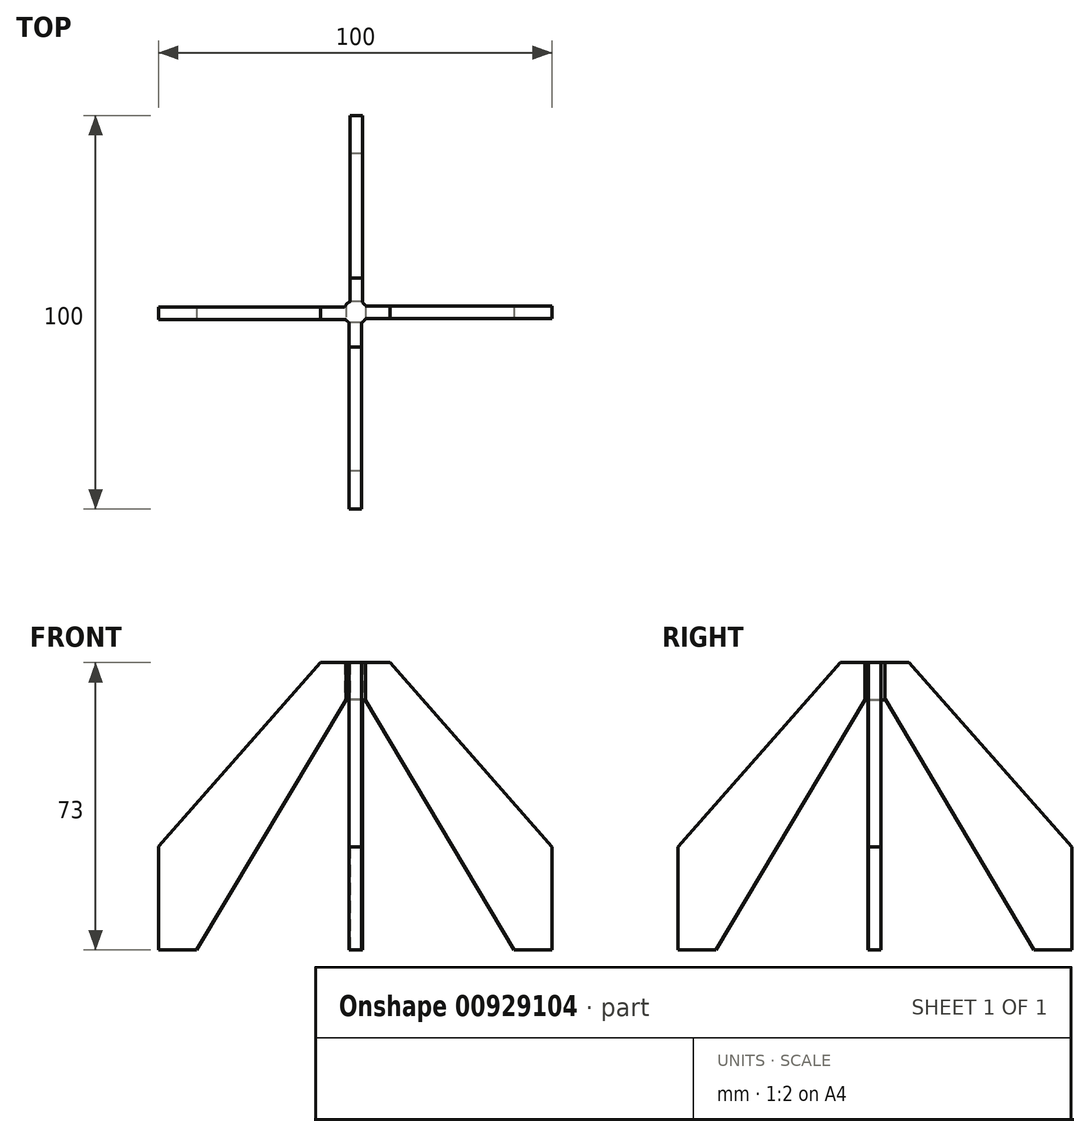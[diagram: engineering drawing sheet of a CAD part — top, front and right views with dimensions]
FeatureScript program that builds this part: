
annotation { "Feature Type Name" : "Feature", "Feature Type Description" : "" }
export const myFeature = defineFeature(function(context is Context, id is Id, definition is map)
    precondition{}
    {
        {
            var Q0;
            Q0=qCreatedBy(makeId("Top.planeOp"),FACE);
            var sketch = newSketch(context, id + "F0", { "sketchPlane" : qUnion([Q0])});
            skCircle(sketch, "E0", {"center": v(0, 0) * mm, "radius": 3.05 * mm});
            skSolve(sketch);
        }
        {
            var Q0;
            Q0=makeQuery(id+"F0.imprint","IMPRINT",FACE,{"disambiguationData":[TD([[makeQuery(id+"F0.imprint","IMPRINT",EDGE,{"derivedFrom":sQuery(id+"F0.wireOp",EDGE,"E0")}),1.0]])]});
            extrude(context, id + "F1", {"entities" : qUnion([Q0]), "depth" : 110 * mm, "offsetDistance" : 25.4 * mm});
        }
        {
            var Q0;
            Q0=qCreatedBy(makeId("Top.planeOp"),FACE);
            var sketch = newSketch(context, id + "F2", { "sketchPlane" : qUnion([Q0])});
            skLineSegment(sketch, "E1.bottom", {"start": v(1.6, 0) * mm, "end": v(-1.58, 0) * mm});
            skLineSegment(sketch, "E1.top", {"start": v(1.6, -50) * mm, "end": v(-1.58, -50) * mm});
            skLineSegment(sketch, "E1.left", {"start": v(1.6, 0) * mm, "end": v(1.6, -50) * mm});
            skLineSegment(sketch, "E1.right", {"start": v(-1.58, 0) * mm, "end": v(-1.58, -50) * mm});
            skSolve(sketch);
        }
        {
            var Q0;
            Q0=makeQuery(id+"F2.imprint","IMPRINT",FACE,{"disambiguationData":[TD([[makeQuery(id+"F2.imprint","IMPRINT",EDGE,{"derivedFrom":sQuery(id+"F2.wireOp",EDGE,"E1.bottom")}),1.0]])]});
            extrude(context, id + "F3", {"entities" : qUnion([Q0]), "operationType" : NewBodyOperationType.ADD, "depth" : 80 * mm, "offsetDistance" : 25.4 * mm});
        }
        {
            var Q0;
            Q0=makeQuery(id+"F3.opExtrude","SWEPT_FACE",FACE,{"disambiguationData":[OSD([sQuery(id+"F2.wireOp",EDGE,"E1.right")])]});
            var sketch = newSketch(context, id + "F4", { "sketchPlane" : qUnion([Q0])});
            skLineSegment(sketch, "E2", {"start": v(2.6, 80) * mm, "end": v(50, 26.2) * mm});
            skSolve(sketch);
        }
        {
            var Q0;
            {var subQ0=sQuery(id+"F4.wireOp",EDGE,"E2");Q0=makeQuery(id+"F4.imprint","IMPRINT",FACE,{"disambiguationData":[TD([[makeQuery(id+"F4.imprint","IMPRINT",EDGE,{"derivedFrom":subQ0}),1.0]])]});}
            extrude(context, id + "F5", {"entities" : qUnion([Q0]), "operationType" : NewBodyOperationType.REMOVE, "endBound" : BoundingType.UP_TO_NEXT, "oppositeDirection" : true, "depth" : 25.4 * mm, "offsetDistance" : 25.4 * mm});
        }
        {
            var Q0;
            Q0=qCreatedBy(makeId("Top.planeOp"),FACE);
            var sketch = newSketch(context, id + "F6", { "sketchPlane" : qUnion([Q0])});
            skLineSegment(sketch, "E3.bottom", {"start": v(0, 1.57) * mm, "end": v(50, 1.57) * mm});
            skLineSegment(sketch, "E3.top", {"start": v(0, -1.6) * mm, "end": v(50, -1.6) * mm});
            skLineSegment(sketch, "E3.left", {"start": v(0, 1.57) * mm, "end": v(0, -1.6) * mm});
            skLineSegment(sketch, "E3.right", {"start": v(50, 1.57) * mm, "end": v(50, -1.6) * mm});
            skSolve(sketch);
        }
        {
            var Q0;
            Q0=makeQuery(id+"F6.imprint","IMPRINT",FACE,{"disambiguationData":[TD([[makeQuery(id+"F6.imprint","IMPRINT",EDGE,{"derivedFrom":sQuery(id+"F6.wireOp",EDGE,"E3.bottom")}),-1.0]])]});
            extrude(context, id + "F7", {"entities" : qUnion([Q0]), "operationType" : NewBodyOperationType.ADD, "depth" : 80 * mm, "offsetDistance" : 25.4 * mm});
        }
        {
            var Q0;
            Q0=makeQuery(id+"F7.opExtrude","SWEPT_FACE",FACE,{"disambiguationData":[OSD([sQuery(id+"F6.wireOp",EDGE,"E3.top")])]});
            var sketch = newSketch(context, id + "F8", { "sketchPlane" : qUnion([Q0])});
            skLineSegment(sketch, "E4", {"start": v(2.59, 80) * mm, "end": v(2.59, 26.17) * mm});
            skLineSegment(sketch, "E5", {"start": v(2.59, 26.17) * mm, "end": v(50, 26.17) * mm});
            skLineSegment(sketch, "E6", {"start": v(50, 26.17) * mm, "end": v(2.59, 80) * mm});
            skSolve(sketch);
        }
        {
            var Q0;
            {var subQ0=sQuery(id+"F8.wireOp",EDGE,"E6");Q0=makeQuery(id+"F8.imprint","IMPRINT",FACE,{"disambiguationData":[TD([[makeQuery(id+"F8.imprint","IMPRINT",EDGE,{"derivedFrom":subQ0}),-1.0]])]});}
            extrude(context, id + "F9", {"entities" : qUnion([Q0]), "operationType" : NewBodyOperationType.REMOVE, "endBound" : BoundingType.UP_TO_NEXT, "oppositeDirection" : true, "depth" : 25.4 * mm, "offsetDistance" : 25.4 * mm});
        }
        {
            var Q0;
            Q0=qCreatedBy(makeId("Top.planeOp"),FACE);
            var sketch = newSketch(context, id + "F10", { "sketchPlane" : qUnion([Q0])});
            skLineSegment(sketch, "E7.bottom", {"start": v(1.78, 0) * mm, "end": v(-1.4, 0) * mm});
            skLineSegment(sketch, "E7.top", {"start": v(1.78, 50) * mm, "end": v(-1.4, 50) * mm});
            skLineSegment(sketch, "E7.left", {"start": v(1.78, 0) * mm, "end": v(1.78, 50) * mm});
            skLineSegment(sketch, "E7.right", {"start": v(-1.4, 0) * mm, "end": v(-1.4, 50) * mm});
            skSolve(sketch);
        }
        {
            var Q0;
            Q0=makeQuery(id+"F10.imprint","IMPRINT",FACE,{"disambiguationData":[TD([[makeQuery(id+"F10.imprint","IMPRINT",EDGE,{"derivedFrom":sQuery(id+"F10.wireOp",EDGE,"E7.bottom")}),-1.0]])]});
            extrude(context, id + "F11", {"entities" : qUnion([Q0]), "operationType" : NewBodyOperationType.ADD, "depth" : 80 * mm, "offsetDistance" : 25.4 * mm});
        }
        {
            var Q0;
            Q0=makeQuery(id+"F11.opExtrude","SWEPT_FACE",FACE,{"disambiguationData":[OSD([sQuery(id+"F10.wireOp",EDGE,"E7.left")])]});
            var sketch = newSketch(context, id + "F12", { "sketchPlane" : qUnion([Q0])});
            skLineSegment(sketch, "E8", {"start": v(2.48, 80) * mm, "end": v(2.48, 26.2) * mm});
            skLineSegment(sketch, "E9", {"start": v(2.48, 26.2) * mm, "end": v(50, 26.2) * mm});
            skLineSegment(sketch, "E10", {"start": v(50, 26.2) * mm, "end": v(2.48, 80) * mm});
            skSolve(sketch);
        }
        {
            var Q0;
            {var subQ0=sQuery(id+"F12.wireOp",EDGE,"E10");Q0=makeQuery(id+"F12.imprint","IMPRINT",FACE,{"disambiguationData":[TD([[makeQuery(id+"F12.imprint","IMPRINT",EDGE,{"derivedFrom":subQ0}),-1.0]])]});}
            extrude(context, id + "F13", {"entities" : qUnion([Q0]), "operationType" : NewBodyOperationType.REMOVE, "endBound" : BoundingType.UP_TO_NEXT, "oppositeDirection" : true, "depth" : 25.4 * mm, "offsetDistance" : 25.4 * mm});
        }
        {
            var Q0;
            Q0=qCreatedBy(makeId("Top.planeOp"),FACE);
            var sketch = newSketch(context, id + "F14", { "sketchPlane" : qUnion([Q0])});
            skLineSegment(sketch, "E11.bottom", {"start": v(0, -1.84) * mm, "end": v(-50, -1.84) * mm});
            skLineSegment(sketch, "E11.top", {"start": v(0, 1.34) * mm, "end": v(-50, 1.34) * mm});
            skLineSegment(sketch, "E11.left", {"start": v(0, -1.84) * mm, "end": v(0, 1.34) * mm});
            skLineSegment(sketch, "E11.right", {"start": v(-50, -1.84) * mm, "end": v(-50, 1.34) * mm});
            skSolve(sketch);
        }
        {
            var Q0;
            Q0=makeQuery(id+"F14.imprint","IMPRINT",FACE,{"disambiguationData":[TD([[makeQuery(id+"F14.imprint","IMPRINT",EDGE,{"derivedFrom":sQuery(id+"F14.wireOp",EDGE,"E11.bottom")}),-1.0]])]});
            extrude(context, id + "F15", {"entities" : qUnion([Q0]), "operationType" : NewBodyOperationType.ADD, "depth" : 80 * mm, "offsetDistance" : 25.4 * mm});
        }
        {
            var Q0;
            Q0=makeQuery(id+"F15.opExtrude","SWEPT_FACE",FACE,{"disambiguationData":[OSD([sQuery(id+"F14.wireOp",EDGE,"E11.top")])]});
            var sketch = newSketch(context, id + "F16", { "sketchPlane" : qUnion([Q0])});
            skLineSegment(sketch, "E12", {"start": v(2.74, 80) * mm, "end": v(2.74, 26.27) * mm});
            skLineSegment(sketch, "E13", {"start": v(2.74, 26.27) * mm, "end": v(50, 26.27) * mm});
            skLineSegment(sketch, "E14", {"start": v(50, 26.27) * mm, "end": v(2.74, 80) * mm});
            skSolve(sketch);
        }
        {
            var Q0;
            {var subQ0=sQuery(id+"F16.wireOp",EDGE,"E14");Q0=makeQuery(id+"F16.imprint","IMPRINT",FACE,{"disambiguationData":[TD([[makeQuery(id+"F16.imprint","IMPRINT",EDGE,{"derivedFrom":subQ0}),-1.0]])]});}
            extrude(context, id + "F17", {"entities" : qUnion([Q0]), "operationType" : NewBodyOperationType.REMOVE, "endBound" : BoundingType.UP_TO_NEXT, "oppositeDirection" : true, "depth" : 25.4 * mm, "offsetDistance" : 25.4 * mm});
        }
        {
            var Q0;
            Q0=makeQuery(id+"F1.opExtrude","CAP_FACE",FACE,{"disambiguationData":[OSD([sQuery(id+"F0.wireOp",EDGE,"E0")])],"isStart":false});
            var sketch = newSketch(context, id + "F18", { "sketchPlane" : qUnion([Q0])});
            skCircle(sketch, "E15", {"center": v(0, 0) * mm, "radius": 5.3 * mm});
            skSolve(sketch);
        }
        {
            var Q0;
            Q0=qSketchRegion(id+"F18",true);
            extrude(context, id + "F19", {"entities" : qUnion([Q0]), "operationType" : NewBodyOperationType.ADD, "depth" : 5 * mm, "offsetDistance" : 25.4 * mm});
        }
        {
            var Q0;
            Q0=makeQuery(id+"F19.opExtrude","CAP_FACE",FACE,{"disambiguationData":[OSD([sQuery(id+"F18.wireOp",EDGE,"E15")])],"isStart":false});
            var sketch = newSketch(context, id + "F20", { "sketchPlane" : qUnion([Q0])});
            skSolve(sketch);
        }
        {
            var Q0;
            Q0=makeQuery(id+"F19.opExtrude","CAP_EDGE",EDGE,{"disambiguationData":[OSD([sQuery(id+"F18.wireOp",EDGE,"E15")])],"isStart":true});
            fillet(context, id + "F21", {"entities" : qUnion([Q0]), "radius" : 5.08 * mm, "tangentPropagation" : true, "allowEdgeOverflow" : false});
        }
        {
            var Q0;
            Q0=makeQuery(id+"F20.imprint","IMPRINT",FACE,{"disambiguationData":[TD([[makeQuery(id+"F20.imprint","IMPRINT",EDGE,{"derivedFrom":makeQuery(id+"F19.opExtrude","CAP_EDGE",EDGE,{"disambiguationData":[OSD([sQuery(id+"F18.wireOp",EDGE,"E15")])],"isStart":false})}),1.0]])]});
            var sketch = newSketch(context, id + "F22", { "sketchPlane" : qUnion([Q0])});
            skCircle(sketch, "E16", {"center": v(0, 0) * mm, "radius": 9.43 * mm});
            skSolve(sketch);
        }
        {
            var Q0;
            Q0=makeQuery(id+"F22.imprint","IMPRINT",FACE,{"disambiguationData":[TD([[makeQuery(id+"F22.imprint","IMPRINT",EDGE,{"derivedFrom":sQuery(id+"F22.wireOp",EDGE,"E16")}),1.0]])]});
            var Q1;
            Q1=makeQuery(id+"F20.imprint","IMPRINT",FACE,{"disambiguationData":[TD([[makeQuery(id+"F20.imprint","IMPRINT",EDGE,{"derivedFrom":makeQuery(id+"F19.opExtrude","CAP_EDGE",EDGE,{"disambiguationData":[OSD([sQuery(id+"F18.wireOp",EDGE,"E15")])],"isStart":false})}),1.0]])]});
            extrude(context, id + "F23", {"entities" : qUnion([Q0, Q1]), "operationType" : NewBodyOperationType.REMOVE, "oppositeDirection" : true, "depth" : 42 * mm, "offsetDistance" : 25.4 * mm});
        }
        {
            var Q0;
            Q0=makeQuery(id+"F7.opExtrude","SWEPT_FACE",FACE,{"disambiguationData":[OSD([sQuery(id+"F6.wireOp",EDGE,"E3.top")])]});
            var sketch = newSketch(context, id + "F24", { "sketchPlane" : qUnion([Q0])});
            skLineSegment(sketch, "E17", {"start": v(2.59, 0) * mm, "end": v(2.59, 51.3) * mm});
            skLineSegment(sketch, "E18", {"start": v(2.59, 63.43) * mm, "end": v(40.35, 0) * mm});
            skLineSegment(sketch, "E19", {"start": v(50, 0) * mm, "end": v(40.35, 0) * mm, "construction": true});
            skSolve(sketch);
        }
        {
            var Q0;
            {var subQ0=sQuery(id+"F24.wireOp",EDGE,"E17");Q0=makeQuery(id+"F24.imprint","IMPRINT",FACE,{"disambiguationData":[TD([[makeQuery(id+"F24.imprint","IMPRINT",EDGE,{"derivedFrom":subQ0}),1.0]])]});}
            extrude(context, id + "F25", {"entities" : qUnion([Q0]), "operationType" : NewBodyOperationType.REMOVE, "endBound" : BoundingType.UP_TO_NEXT, "oppositeDirection" : true, "depth" : 25.4 * mm, "offsetDistance" : 25.4 * mm});
        }
        {
            var Q0;
            Q0=makeQuery(id+"F15.opExtrude","SWEPT_FACE",FACE,{"disambiguationData":[OSD([sQuery(id+"F14.wireOp",EDGE,"E11.bottom")])]});
            var sketch = newSketch(context, id + "F26", { "sketchPlane" : qUnion([Q0])});
            skLineSegment(sketch, "E20", {"start": v(-50, 13.13) * mm, "end": v(-40.34, 13.13) * mm, "construction": true});
            skLineSegment(sketch, "E21", {"start": v(-40.34, 0) * mm, "end": v(-2.43, 63.57) * mm});
            skSolve(sketch);
        }
        {
            var Q0;
            {var subQ0=sQuery(id+"F26.wireOp",EDGE,"E21");Q0=makeQuery(id+"F26.imprint","IMPRINT",FACE,{"disambiguationData":[TD([[makeQuery(id+"F26.imprint","IMPRINT",EDGE,{"derivedFrom":subQ0}),-1.0]])]});}
            extrude(context, id + "F27", {"entities" : qUnion([Q0]), "operationType" : NewBodyOperationType.REMOVE, "endBound" : BoundingType.UP_TO_NEXT, "oppositeDirection" : true, "depth" : 25.4 * mm, "offsetDistance" : 25.4 * mm});
        }
        {
            var Q0;
            Q0=makeQuery(id+"F3.opExtrude","SWEPT_FACE",FACE,{"disambiguationData":[OSD([sQuery(id+"F2.wireOp",EDGE,"E1.right")])]});
            var sketch = newSketch(context, id + "F28", { "sketchPlane" : qUnion([Q0])});
            skLineSegment(sketch, "E22", {"start": v(50, 9.83) * mm, "end": v(40.35, 9.83) * mm, "construction": true});
            skLineSegment(sketch, "E23", {"start": v(40.35, 0) * mm, "end": v(2.6, 63.53) * mm});
            skSolve(sketch);
        }
        {
            var Q0;
            {var subQ0=sQuery(id+"F28.wireOp",EDGE,"E23");Q0=makeQuery(id+"F28.imprint","IMPRINT",FACE,{"disambiguationData":[TD([[makeQuery(id+"F28.imprint","IMPRINT",EDGE,{"derivedFrom":subQ0}),1.0]])]});}
            extrude(context, id + "F29", {"entities" : qUnion([Q0]), "operationType" : NewBodyOperationType.REMOVE, "endBound" : BoundingType.UP_TO_NEXT, "oppositeDirection" : true, "depth" : 25.4 * mm, "offsetDistance" : 25.4 * mm});
        }
        {
            var Q0;
            Q0=makeQuery(id+"F11.opExtrude","SWEPT_FACE",FACE,{"disambiguationData":[OSD([sQuery(id+"F10.wireOp",EDGE,"E7.right")])]});
            var sketch = newSketch(context, id + "F30", { "sketchPlane" : qUnion([Q0])});
            skLineSegment(sketch, "E24", {"start": v(-50, 7.52) * mm, "end": v(-40.35, 7.52) * mm, "construction": true});
            skLineSegment(sketch, "E25", {"start": v(-40.35, 0) * mm, "end": v(-2.7, 63.7) * mm});
            skSolve(sketch);
        }
        {
            var Q0;
            {var subQ0=sQuery(id+"F30.wireOp",EDGE,"E25");Q0=makeQuery(id+"F30.imprint","IMPRINT",FACE,{"disambiguationData":[TD([[makeQuery(id+"F30.imprint","IMPRINT",EDGE,{"derivedFrom":subQ0}),-1.0]])]});}
            extrude(context, id + "F31", {"entities" : qUnion([Q0]), "operationType" : NewBodyOperationType.REMOVE, "endBound" : BoundingType.UP_TO_NEXT, "oppositeDirection" : true, "depth" : 25.4 * mm, "offsetDistance" : 25.4 * mm});
        }
        {
            var Q0;
            {var subQ0=sQuery(id+"F6.wireOp",EDGE,"E3.top");var subQ1=sQuery(id+"F0.wireOp",EDGE,"E0");var subQ4=sQuery(id+"F2.wireOp",EDGE,"E1.right");var subQ6=sQuery(id+"F2.wireOp",EDGE,"E1.left");var subQ8=sQuery(id+"F10.wireOp",EDGE,"E7.left");var subQ10=makeQuery(id+"F1.opExtrude","SWEPT_FACE",FACE,{"disambiguationData":[OSD([subQ1])]});var subQ11=sQuery(id+"F14.wireOp",EDGE,"E11.bottom");var subQ14=sQuery(id+"F10.wireOp",EDGE,"E7.right");var subQ15=sQuery(id+"F10.wireOp",EDGE,"E7.top");var subQ19=sQuery(id+"F2.wireOp",EDGE,"E1.top");var subQ21=sQuery(id+"F14.wireOp",EDGE,"E11.top");var subQ22=sQuery(id+"F14.wireOp",EDGE,"E11.right");Q0=makeQuery(id+"F31.boolean.opBoolean","SPLIT",FACE,{"disambiguationData":[TD([subQ10])],"derivedFrom":makeQuery(id+"F29.boolean.opBoolean","SPLIT",FACE,{"disambiguationData":[TD([subQ10])],"derivedFrom":makeQuery(id+"F27.boolean.opBoolean","SPLIT",FACE,{"disambiguationData":[TD([subQ10])],"derivedFrom":makeQuery(id+"F25.boolean.opBoolean","SPLIT",FACE,{"disambiguationData":[TD([subQ10])],"derivedFrom":makeQuery(id+"F15.boolean.opBoolean","MERGE",FACE,{"derivedFrom":[makeQuery(id+"F11.boolean.opBoolean","MERGE",FACE,{"derivedFrom":[makeQuery(id+"F7.boolean.opBoolean","MERGE",FACE,{"derivedFrom":[makeQuery(id+"F3.boolean.opBoolean","MERGE",FACE,{"derivedFrom":[makeQuery(id+"F1.opExtrude","CAP_FACE",FACE,{"disambiguationData":[OSD([subQ1])],"isStart":true}),makeQuery(id+"F3.opExtrude","CAP_FACE",FACE,{"disambiguationData":[OSD([sQuery(id+"F2.wireOp",EDGE,"E1.bottom"),subQ19,subQ6,subQ4])],"isStart":true})]}),makeQuery(id+"F7.opExtrude","CAP_FACE",FACE,{"disambiguationData":[OSD([sQuery(id+"F6.wireOp",EDGE,"E3.bottom"),subQ0,sQuery(id+"F6.wireOp",EDGE,"E3.left"),sQuery(id+"F6.wireOp",EDGE,"E3.right")])],"isStart":true})]}),makeQuery(id+"F11.opExtrude","CAP_FACE",FACE,{"disambiguationData":[OSD([sQuery(id+"F10.wireOp",EDGE,"E7.bottom"),subQ15,subQ8,subQ14])],"isStart":true})]}),makeQuery(id+"F15.opExtrude","CAP_FACE",FACE,{"disambiguationData":[OSD([subQ11,subQ21,sQuery(id+"F14.wireOp",EDGE,"E11.left"),subQ22])],"isStart":true})]})})})})});}
            extrude(context, id + "F32", {"entities" : qUnion([Q0]), "operationType" : NewBodyOperationType.REMOVE, "oppositeDirection" : true, "depth" : 63.5 * mm, "offsetDistance" : 25.4 * mm});
        }
    });
